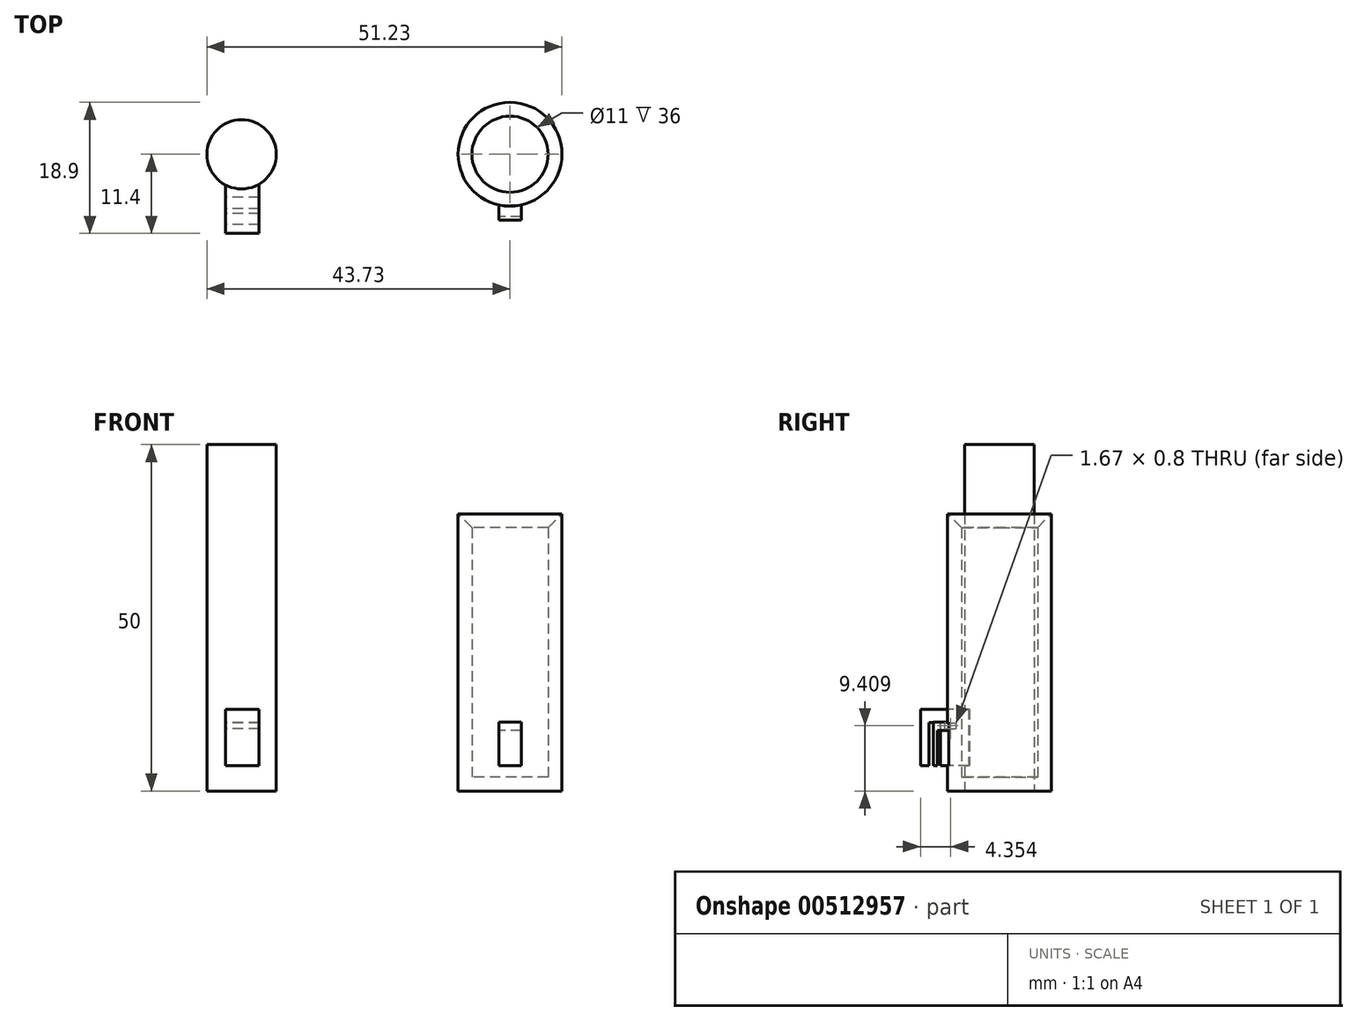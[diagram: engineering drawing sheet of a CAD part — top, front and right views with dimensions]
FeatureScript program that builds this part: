
annotation { "Feature Type Name" : "Feature", "Feature Type Description" : "" }
export const myFeature = defineFeature(function(context is Context, id is Id, definition is map)
    precondition{}
    {
        {
            var Q0;
            Q0=qCreatedBy(makeId("Top.planeOp"),FACE);
            var sketch = newSketch(context, id + "F0", { "sketchPlane" : qUnion([Q0])});
            skCircle(sketch, "E0", {"center": v(0, 0) * mm, "radius": 7.5 * mm});
            skCircle(sketch, "E1", {"center": v(-38.73, 0) * mm, "radius": 5 * mm});
            skSolve(sketch);
        }
        {
            var Q0;
            Q0=makeQuery(id+"F0.imprint","IMPRINT",FACE,{"disambiguationData":[TD([[makeQuery(id+"F0.imprint","IMPRINT",EDGE,{"derivedFrom":sQuery(id+"F0.wireOp",EDGE,"E0")}),1.0]])]});
            extrude(context, id + "F1", {"entities" : qUnion([Q0]), "depth" : 40 * mm});
        }
        {
            var Q0;
            Q0=makeQuery(id+"F0.imprint","IMPRINT",FACE,{"disambiguationData":[TD([[makeQuery(id+"F0.imprint","IMPRINT",EDGE,{"derivedFrom":sQuery(id+"F0.wireOp",EDGE,"E1")}),1.0]])]});
            extrude(context, id + "F2", {"entities" : qUnion([Q0]), "depth" : 50 * mm});
        }
        {
            var Q0;
            Q0=makeQuery(id+"F1.opExtrude","CAP_FACE",FACE,{"disambiguationData":[OSD([sQuery(id+"F0.wireOp",EDGE,"E0")])],"isStart":false});
            shell(context, id + "F3", {"entities" : qUnion([Q0]), "thickness" : 2 * mm});
        }
        {
            var Q0;
            Q0=qCreatedBy(makeId("Front.planeOp"),FACE);
            cPlane(context, id + "F4", {"entities" : qUnion([Q0]), "cplaneType" : CPlaneType.OFFSET, "offset" : 7.5 * mm, "width" : 150 * mm, "height" : 150 * mm});
        }
        {
            var Q0;
            Q0=qCreatedBy(id+"F4.planeOp",FACE);
            var sketch = newSketch(context, id + "F5", { "sketchPlane" : qUnion([Q0])});
            skLineSegment(sketch, "E2.bottom", {"start": v(-1.63, 9.95) * mm, "end": v(1.63, 9.95) * mm});
            skLineSegment(sketch, "E2.top", {"start": v(-1.63, 3.63) * mm, "end": v(1.63, 3.63) * mm});
            skLineSegment(sketch, "E2.left", {"start": v(-1.63, 9.95) * mm, "end": v(-1.63, 3.63) * mm});
            skLineSegment(sketch, "E2.right", {"start": v(1.63, 9.95) * mm, "end": v(1.63, 3.63) * mm});
            skPoint(sketch, "E2.middle", {"position": v(0, 6.8) * mm});
            skLineSegment(sketch, "E3.bottom", {"start": v(-41.04, 11.81) * mm, "end": v(-36.2, 11.81) * mm});
            skLineSegment(sketch, "E3.top", {"start": v(-41.04, 3.63) * mm, "end": v(-36.2, 3.63) * mm});
            skLineSegment(sketch, "E3.left", {"start": v(-41.04, 11.81) * mm, "end": v(-41.04, 3.63) * mm});
            skLineSegment(sketch, "E3.right", {"start": v(-36.2, 11.81) * mm, "end": v(-36.2, 3.63) * mm});
            skPoint(sketch, "E3.middle", {"position": v(-38.62, 7.72) * mm});
            skSolve(sketch);
        }
        {
            var Q0;
            Q0=makeQuery(id+"F5.imprint","IMPRINT",FACE,{"disambiguationData":[TD([[makeQuery(id+"F5.imprint","IMPRINT",EDGE,{"derivedFrom":sQuery(id+"F5.wireOp",EDGE,"E3.bottom")}),-1.0]])]});
            extrude(context, id + "F6", {"entities" : qUnion([Q0]), "operationType" : NewBodyOperationType.ADD, "endBound" : BoundingType.SYMMETRIC, "oppositeDirection" : true, "depth" : 7.8 * mm, "offsetDistance" : 25 * mm});
        }
        {
            var Q0;
            Q0=makeQuery(id+"F5.imprint","IMPRINT",FACE,{"disambiguationData":[TD([[makeQuery(id+"F5.imprint","IMPRINT",EDGE,{"derivedFrom":sQuery(id+"F5.wireOp",EDGE,"E2.bottom")}),-1.0]])]});
            extrude(context, id + "F7", {"entities" : qUnion([Q0]), "operationType" : NewBodyOperationType.ADD, "endBound" : BoundingType.SYMMETRIC, "depth" : 4 * mm});
        }
        {
            var Q0;
            Q0=makeQuery(id+"F6.opExtrude","SWEPT_FACE",FACE,{"disambiguationData":[OSD([sQuery(id+"F5.wireOp",EDGE,"E3.left")])]});
            var sketch = newSketch(context, id + "F8", { "sketchPlane" : qUnion([Q0])});
            skLineSegment(sketch, "E4.bottom", {"start": v(8.93, 3.63) * mm, "end": v(6.83, 3.63) * mm});
            skLineSegment(sketch, "E4.top", {"start": v(8.93, 9.81) * mm, "end": v(6.83, 9.81) * mm});
            skLineSegment(sketch, "E4.left", {"start": v(8.93, 3.63) * mm, "end": v(8.93, 9.81) * mm});
            skLineSegment(sketch, "E4.right", {"start": v(6.83, 3.63) * mm, "end": v(6.83, 9.81) * mm});
            skPoint(sketch, "E5.firstSnap0", {"position": v(7.88, 9.81) * mm});
            skLineSegment(sketch, "E5.bottom", {"start": v(7.88, 9) * mm, "end": v(6.21, 9) * mm});
            skLineSegment(sketch, "E5.top", {"start": v(7.88, 9.81) * mm, "end": v(6.21, 9.81) * mm});
            skLineSegment(sketch, "E5.left", {"start": v(7.88, 9) * mm, "end": v(7.88, 9.81) * mm});
            skLineSegment(sketch, "E5.right", {"start": v(6.21, 9) * mm, "end": v(6.21, 9.81) * mm});
            skSolve(sketch);
        }
        {
            var Q0;
            {var subQ1=sQuery(id+"F8.wireOp",EDGE,"E4.bottom");Q0=makeQuery(id+"F8.imprint","IMPRINT",FACE,{"disambiguationData":[TD([[makeQuery(id+"F8.imprint","IMPRINT",EDGE,{"derivedFrom":subQ1}),-1.0]])]});}
            var Q1;
            {var subQ5=sQuery(id+"F8.wireOp",EDGE,"E5.left");Q1=makeQuery(id+"F8.imprint","IMPRINT",FACE,{"disambiguationData":[TD([[makeQuery(id+"F8.imprint","IMPRINT",EDGE,{"derivedFrom":subQ5}),1.0]])]});}
            var Q2;
            {var subQ5=sQuery(id+"F8.wireOp",EDGE,"E5.right");Q2=makeQuery(id+"F8.imprint","IMPRINT",FACE,{"disambiguationData":[TD([[makeQuery(id+"F8.imprint","IMPRINT",EDGE,{"derivedFrom":subQ5}),-1.0]])]});}
            extrude(context, id + "F9", {"entities" : qUnion([Q0, Q1, Q2]), "operationType" : NewBodyOperationType.REMOVE, "endBound" : BoundingType.UP_TO_NEXT, "oppositeDirection" : true, "depth" : 25 * mm});
        }
        {
            var Q0;
            Q0=makeQuery(id+"F7.opExtrude","SWEPT_FACE",FACE,{"disambiguationData":[OSD([sQuery(id+"F5.wireOp",EDGE,"E2.left")])]});
            var sketch = newSketch(context, id + "F10", { "sketchPlane" : qUnion([Q0])});
            skLineSegment(sketch, "E6.bottom", {"start": v(8.98, 3.63) * mm, "end": v(7.32, 3.63) * mm});
            skLineSegment(sketch, "E6.top", {"start": v(8.98, 8.72) * mm, "end": v(7.32, 8.72) * mm});
            skLineSegment(sketch, "E6.left", {"start": v(8.98, 3.63) * mm, "end": v(8.98, 8.72) * mm});
            skLineSegment(sketch, "E6.right", {"start": v(7.32, 3.63) * mm, "end": v(7.32, 8.72) * mm});
            skSolve(sketch);
        }
        {
            var Q0;
            Q0=makeQuery(id+"F10.imprint","IMPRINT",FACE,{"disambiguationData":[TD([[makeQuery(id+"F10.imprint","IMPRINT",EDGE,{"derivedFrom":sQuery(id+"F10.wireOp",EDGE,"E6.bottom")}),-1.0]])]});
            extrude(context, id + "F11", {"entities" : qUnion([Q0]), "operationType" : NewBodyOperationType.REMOVE, "endBound" : BoundingType.UP_TO_NEXT, "oppositeDirection" : true, "depth" : 25 * mm});
        }
        {
            var Q0;
            {var subQ0=sQuery(id+"F0.wireOp",EDGE,"E0");Q0=makeQuery(id+"F3.opShell","OFFSET_EDGE",EDGE,{"disambiguationData":[OSD([subQ0]),TDD([makeQuery(id+"F1.opExtrude","CAP_EDGE",EDGE,{"disambiguationData":[OSD([subQ0])],"isStart":false})])]});}
            chamfer(context, id + "F12", {"entities" : qUnion([Q0]), "width" : 2 * mm, "tangentPropagation" : true});
        }
        {
            var Q0;
            Q0=makeQuery(id+"F6.opExtrude","SWEPT_FACE",FACE,{"disambiguationData":[OSD([sQuery(id+"F5.wireOp",EDGE,"E3.left")])]});
            var sketch = newSketch(context, id + "F13", { "sketchPlane" : qUnion([Q0])});
            skLineSegment(sketch, "E7.bottom", {"start": v(10.15, 9.86) * mm, "end": v(8.54, 9.86) * mm});
            skLineSegment(sketch, "E7.top", {"start": v(10.15, 1.93) * mm, "end": v(8.54, 1.93) * mm});
            skLineSegment(sketch, "E7.left", {"start": v(10.15, 9.86) * mm, "end": v(10.15, 1.93) * mm});
            skLineSegment(sketch, "E7.right", {"start": v(8.54, 9.86) * mm, "end": v(8.54, 1.93) * mm});
            skSolve(sketch);
        }
        {
            var Q0;
            {var subQ0=sQuery(id+"F13.wireOp",EDGE,"E7.bottom");Q0=makeQuery(id+"F13.imprint","IMPRINT",FACE,{"disambiguationData":[TD([[makeQuery(id+"F13.imprint","IMPRINT",EDGE,{"derivedFrom":subQ0}),1.0]])]});}
            extrude(context, id + "F14", {"entities" : qUnion([Q0]), "operationType" : NewBodyOperationType.REMOVE, "endBound" : BoundingType.UP_TO_NEXT, "oppositeDirection" : true, "depth" : 25 * mm, "offsetDistance" : 25 * mm});
        }
    });
